# Revit family: 2-6165-124 Dione
name_source: partatom
category: Lighting Fixtures
revit_build: Autodesk Revit LT 2014 (Build: 20130308_1515(x64)
units: mm (PartAtom-declared; Revit-internal decimal feet)

## types (1)
- 2-6165-124 Dione
    ADA Compliant = Yes
    Apparent Load = 50 VA
    Color Filter = 16777215
    Default Elevation = 4' - 0"
    Description = 21" dia. ceiling mount
    Diffuser = 1 - Frosted Glass
    Dimming Lamp Color Temperature Shift = <None>
    Emit Shape Visible in Rendering = No
    Emit from Circle Diameter = 2' - 0"
    Fixture Diameter = 1' - 9 1/16"
    Input Power = 49.9
    Input Voltage = 120V
    Junction Box = 4" Octagonal
    Lamp = 1x55W T5 circline fluorescent 2Gx13
    Lamp Manufacturer = Sylvania
    Manufacturer = Oxygen Lighting
    Metal Finish = 24 - Satin Nickel
    Model = 2-6165-124
    Photometric Web File = 2-6165-124.IES
    Power Factor = 0.99
    Tilt Angle = 180.00°
    Type Comments = Lighting - Fluorescent
    URL = http:www//oxygenlighting.com

## geometry (parser evidence)
native form markers: Sweep x1
no freeform markers — native parametric forms only
